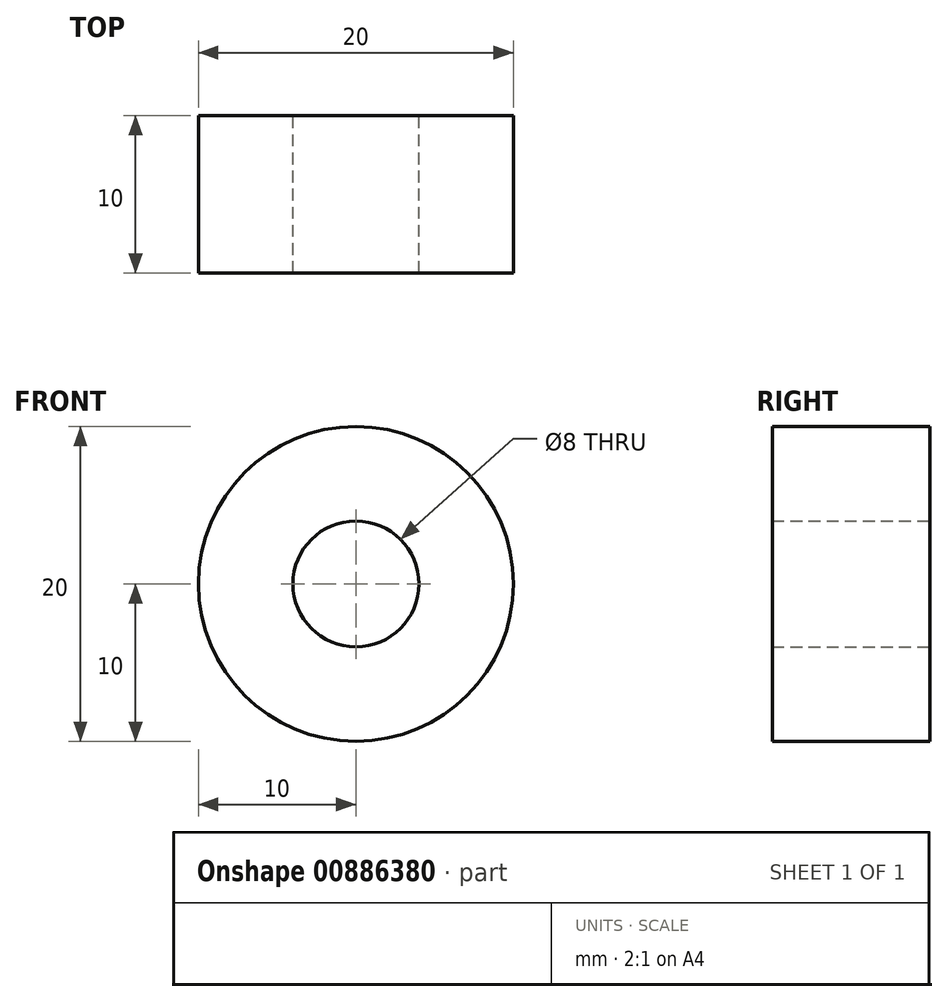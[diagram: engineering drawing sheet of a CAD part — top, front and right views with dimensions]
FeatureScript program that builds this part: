
annotation { "Feature Type Name" : "Feature", "Feature Type Description" : "" }
export const myFeature = defineFeature(function(context is Context, id is Id, definition is map)
    precondition{}
    {
        {
            var Q0;
            Q0=qCreatedBy(makeId("Front.planeOp"),FACE);
            var sketch = newSketch(context, id + "F0", { "sketchPlane" : qUnion([Q0])});
            skCircle(sketch, "E0", {"center": v(0, 0) * mm, "radius": 10 * mm});
            skCircle(sketch, "E1", {"center": v(0, 0) * mm, "radius": 4 * mm});
            skSolve(sketch);
        }
        {
            var Q0;
            Q0 = qSketchRegion(id + "F0", true);
            extrude(context, id + "F1", {"entities" : qUnion([Q0]), "depth" : 10 * mm, "offsetDistance" : 25 * mm});
        }
    });
